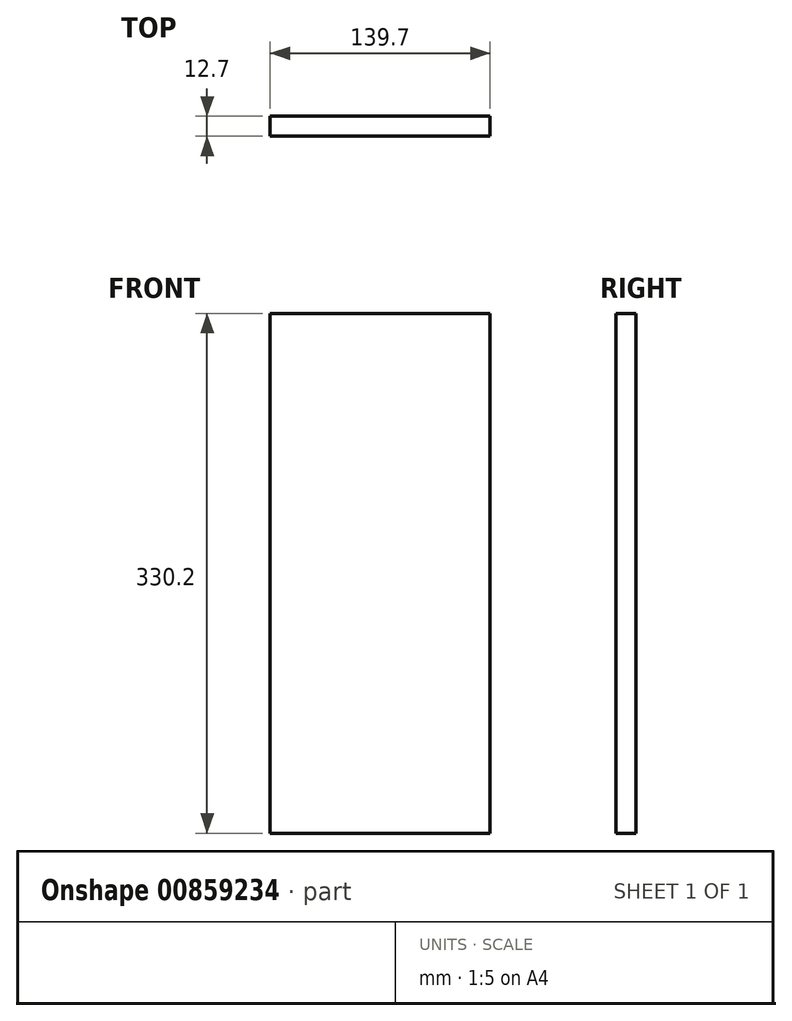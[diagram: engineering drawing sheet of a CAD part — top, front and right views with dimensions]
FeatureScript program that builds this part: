
annotation { "Feature Type Name" : "Feature", "Feature Type Description" : "" }
export const myFeature = defineFeature(function(context is Context, id is Id, definition is map)
    precondition{}
    {
        {
            var Q0;
            Q0=qCreatedBy(makeId("Front.planeOp"),FACE);
            var sketch = newSketch(context, id + "F0", { "sketchPlane" : qUnion([Q0])});
            skLineSegment(sketch, "E0.bottom", {"start": v(0, 0) * mm, "end": v(-139.7, 0) * mm});
            skLineSegment(sketch, "E0.top", {"start": v(0, 330.2) * mm, "end": v(-139.7, 330.2) * mm});
            skLineSegment(sketch, "E0.left", {"start": v(0, 0) * mm, "end": v(0, 330.2) * mm});
            skLineSegment(sketch, "E0.right", {"start": v(-139.7, 0) * mm, "end": v(-139.7, 330.2) * mm});
            skSolve(sketch);
        }
        {
            var Q0;
            Q0 = qSketchRegion(id + "F0", true);
            extrude(context, id + "F1", {"entities" : qUnion([Q0]), "depth" : 12.7 * mm, "offsetDistance" : 25.4 * mm});
        }
    });
